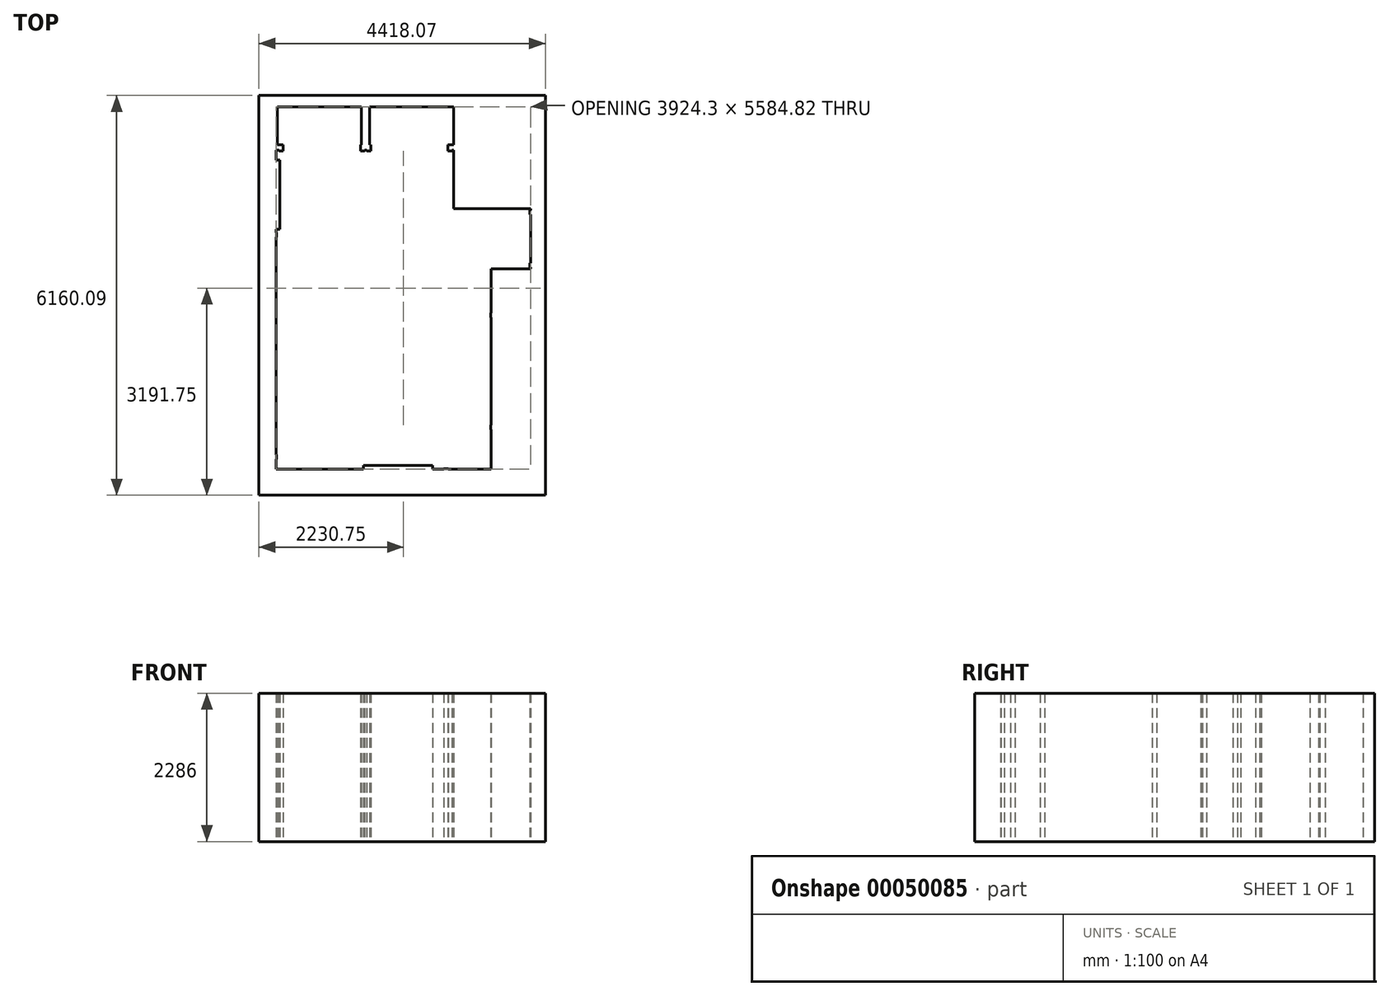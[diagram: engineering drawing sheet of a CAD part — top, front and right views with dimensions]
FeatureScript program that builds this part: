
annotation { "Feature Type Name" : "Feature", "Feature Type Description" : "" }
export const myFeature = defineFeature(function(context is Context, id is Id, definition is map)
    precondition{}
    {
        {
            var Q0;
            Q0=qCreatedBy(makeId("Top.planeOp"),FACE);
            var sketch = newSketch(context, id + "F0", { "sketchPlane" : qUnion([Q0])});
            skLineSegment(sketch, "E0", {"start": v(5358.14, -661.23) * mm, "end": v(4748.54, -661.23) * mm});
            skLineSegment(sketch, "E1", {"start": v(1452.89, 1837.5) * mm, "end": v(2748.29, 1837.5) * mm});
            skLineSegment(sketch, "E2.trimOffspring", {"start": v(2875.29, 1837.5) * mm, "end": v(4170.69, 1837.5) * mm});
            skLineSegment(sketch, "E3", {"start": v(1452.89, 1837.5) * mm, "end": v(1452.89, 1253.3) * mm});
            skLineSegment(sketch, "E4", {"start": v(1452.89, 1253.3) * mm, "end": v(1541.79, 1253.3) * mm});
            skLineSegment(sketch, "E5", {"start": v(4170.69, 1837.5) * mm, "end": v(4170.69, 1253.3) * mm});
            skLineSegment(sketch, "E6", {"start": v(4170.69, 1253.3) * mm, "end": v(4081.79, 1253.3) * mm});
            skLineSegment(sketch, "E7", {"start": v(4170.69, 1170.75) * mm, "end": v(4170.69, 269.05) * mm});
            skLineSegment(sketch, "E8", {"start": v(4170.69, 269.05) * mm, "end": v(5358.14, 269.05) * mm});
            skLineSegment(sketch, "E9", {"start": v(4748.54, -661.23) * mm, "end": v(4748.54, -1340.68) * mm});
            skLineSegment(sketch, "E10", {"start": v(4748.54, -1340.68) * mm, "end": v(4742.19, -1340.68) * mm});
            skLineSegment(sketch, "E11", {"start": v(4742.19, -1340.68) * mm, "end": v(4742.19, -1410.53) * mm});
            skLineSegment(sketch, "E12", {"start": v(4742.19, -1410.53) * mm, "end": v(4748.54, -1410.53) * mm});
            skLineSegment(sketch, "E13", {"start": v(4748.54, -1410.53) * mm, "end": v(4748.54, -3067.88) * mm});
            skLineSegment(sketch, "E14", {"start": v(4748.54, -3067.88) * mm, "end": v(4742.19, -3067.88) * mm});
            skLineSegment(sketch, "E15", {"start": v(4742.19, -3067.88) * mm, "end": v(4742.19, -3137.73) * mm});
            skLineSegment(sketch, "E16", {"start": v(4742.19, -3137.73) * mm, "end": v(4748.54, -3137.73) * mm});
            skLineSegment(sketch, "E17", {"start": v(4748.54, -3137.73) * mm, "end": v(4748.54, -3747.33) * mm});
            skLineSegment(sketch, "E18", {"start": v(4748.54, -3747.33) * mm, "end": v(4088.14, -3747.33) * mm});
            skLineSegment(sketch, "E19", {"start": v(4088.14, -3747.33) * mm, "end": v(4088.14, -3740.98) * mm});
            skLineSegment(sketch, "E20", {"start": v(4088.14, -3740.98) * mm, "end": v(4018.29, -3740.98) * mm});
            skLineSegment(sketch, "E21", {"start": v(4018.29, -3740.98) * mm, "end": v(4018.29, -3747.33) * mm});
            skLineSegment(sketch, "E22", {"start": v(1433.84, 1170.75) * mm, "end": v(1433.84, 1018.35) * mm});
            skLineSegment(sketch, "E23", {"start": v(1433.84, 1018.35) * mm, "end": v(1490.99, 1018.35) * mm});
            skLineSegment(sketch, "E24", {"start": v(1490.99, 1018.35) * mm, "end": v(1490.99, -48.45) * mm});
            skLineSegment(sketch, "E25", {"start": v(1490.99, -48.45) * mm, "end": v(1433.84, -48.45) * mm});
            skLineSegment(sketch, "E26", {"start": v(1433.84, -48.45) * mm, "end": v(1433.84, -99.25) * mm});
            skLineSegment(sketch, "E27", {"start": v(1433.84, -99.25) * mm, "end": v(1440.19, -99.25) * mm});
            skLineSegment(sketch, "E28", {"start": v(1440.19, -99.25) * mm, "end": v(1440.19, -169.1) * mm});
            skLineSegment(sketch, "E29", {"start": v(1440.19, -169.1) * mm, "end": v(1433.84, -169.1) * mm});
            skLineSegment(sketch, "E30", {"start": v(1433.84, -169.1) * mm, "end": v(1433.84, -3525.08) * mm});
            skLineSegment(sketch, "E31", {"start": v(1433.84, -3525.08) * mm, "end": v(1440.19, -3525.08) * mm});
            skLineSegment(sketch, "E32", {"start": v(1440.19, -3525.08) * mm, "end": v(1440.19, -3594.93) * mm});
            skLineSegment(sketch, "E33", {"start": v(1440.19, -3594.93) * mm, "end": v(1433.84, -3594.93) * mm});
            skLineSegment(sketch, "E34", {"start": v(1433.84, -3594.93) * mm, "end": v(1433.84, -3747.33) * mm});
            skLineSegment(sketch, "E35", {"start": v(4018.29, -3747.33) * mm, "end": v(3846.84, -3747.33) * mm});
            skLineSegment(sketch, "E36", {"start": v(3846.84, -3747.33) * mm, "end": v(3846.84, -3690.18) * mm});
            skLineSegment(sketch, "E37", {"start": v(3846.84, -3690.18) * mm, "end": v(2780.04, -3690.18) * mm});
            skLineSegment(sketch, "E38", {"start": v(2780.04, -3690.18) * mm, "end": v(2780.04, -3747.33) * mm});
            skLineSegment(sketch, "E39", {"start": v(2780.04, -3747.33) * mm, "end": v(1433.84, -3747.33) * mm});
            skLineSegment(sketch, "E40", {"start": v(2732.41, 1154.87) * mm, "end": v(2795.91, 1154.87) * mm});
            skLineSegment(sketch, "E41", {"start": v(2795.91, 1154.87) * mm, "end": v(2795.91, 1170.75) * mm});
            skLineSegment(sketch, "E42", {"start": v(2795.91, 1170.75) * mm, "end": v(2827.66, 1170.75) * mm});
            skLineSegment(sketch, "E43", {"start": v(2827.66, 1170.75) * mm, "end": v(2827.66, 1154.87) * mm});
            skLineSegment(sketch, "E44", {"start": v(2827.66, 1154.87) * mm, "end": v(2891.16, 1154.87) * mm});
            skLineSegment(sketch, "E45", {"start": v(2732.41, 1154.87) * mm, "end": v(2732.41, 1253.3) * mm});
            skLineSegment(sketch, "E46", {"start": v(2732.41, 1253.3) * mm, "end": v(2748.29, 1253.3) * mm});
            skLineSegment(sketch, "E47", {"start": v(2748.29, 1253.3) * mm, "end": v(2748.29, 1837.5) * mm});
            skLineSegment(sketch, "E48", {"start": v(2875.29, 1837.5) * mm, "end": v(2875.29, 1253.3) * mm});
            skLineSegment(sketch, "E49", {"start": v(2875.29, 1253.3) * mm, "end": v(2891.16, 1253.3) * mm});
            skLineSegment(sketch, "E50", {"start": v(2891.16, 1253.3) * mm, "end": v(2891.16, 1154.87) * mm});
            skLineSegment(sketch, "E51", {"start": v(4081.79, 1253.3) * mm, "end": v(4081.79, 1154.87) * mm});
            skLineSegment(sketch, "E52", {"start": v(4081.79, 1154.87) * mm, "end": v(4145.29, 1154.87) * mm});
            skLineSegment(sketch, "E53", {"start": v(4145.29, 1154.87) * mm, "end": v(4145.29, 1170.75) * mm});
            skLineSegment(sketch, "E54", {"start": v(4145.29, 1170.75) * mm, "end": v(4170.69, 1170.75) * mm});
            skLineSegment(sketch, "E55", {"start": v(1478.29, 1170.75) * mm, "end": v(1478.29, 1154.87) * mm});
            skLineSegment(sketch, "E56", {"start": v(1478.29, 1154.87) * mm, "end": v(1541.79, 1154.87) * mm});
            skLineSegment(sketch, "E57", {"start": v(1541.79, 1154.87) * mm, "end": v(1541.79, 1253.3) * mm});
            skLineSegment(sketch, "E58", {"start": v(1433.84, 1170.75) * mm, "end": v(1478.29, 1170.75) * mm});
            skLineSegment(sketch, "E59", {"start": v(5358.14, 269.05) * mm, "end": v(5358.14, 243.65) * mm});
            skLineSegment(sketch, "E60", {"start": v(5358.14, 243.65) * mm, "end": v(5342.26, 243.65) * mm});
            skLineSegment(sketch, "E61", {"start": v(5342.26, 243.65) * mm, "end": v(5342.26, 180.15) * mm});
            skLineSegment(sketch, "E62", {"start": v(5342.26, 180.15) * mm, "end": v(5358.14, 180.15) * mm});
            skLineSegment(sketch, "E63", {"start": v(5358.14, 180.15) * mm, "end": v(5358.14, -572.33) * mm});
            skLineSegment(sketch, "E64", {"start": v(5358.14, -572.33) * mm, "end": v(5342.26, -572.33) * mm});
            skLineSegment(sketch, "E65", {"start": v(5342.26, -572.33) * mm, "end": v(5342.26, -635.83) * mm});
            skLineSegment(sketch, "E66", {"start": v(5342.26, -635.83) * mm, "end": v(5358.14, -635.83) * mm});
            skLineSegment(sketch, "E67", {"start": v(5358.14, -635.83) * mm, "end": v(5358.14, -661.23) * mm});
            skLineSegment(sketch, "E68", {"start": v(1266.77, 2013.42) * mm, "end": v(5583.3, 2013.42) * mm});
            skLineSegment(sketch, "E69", {"start": v(5583.3, 2013.42) * mm, "end": v(5583.3, -4146.67) * mm});
            skLineSegment(sketch, "E70", {"start": v(5583.3, -4146.67) * mm, "end": v(1165.24, -4146.67) * mm});
            skLineSegment(sketch, "E71", {"start": v(1165.24, -4146.67) * mm, "end": v(1165.24, 2013.42) * mm});
            skLineSegment(sketch, "E72", {"start": v(1165.24, 2013.42) * mm, "end": v(1266.77, 2013.42) * mm});
            skSolve(sketch);
        }
        {
            var Q0;
            Q0=makeQuery(id+"F0.imprint","IMPRINT",FACE,{"disambiguationData":[TD([[makeQuery(id+"F0.imprint","IMPRINT",EDGE,{"derivedFrom":sQuery(id+"F0.wireOp",EDGE,"E0")}),1.0]])]});
            extrude(context, id + "F1", {"entities" : qUnion([Q0]), "depth" : 2286 * mm});
        }
    });
